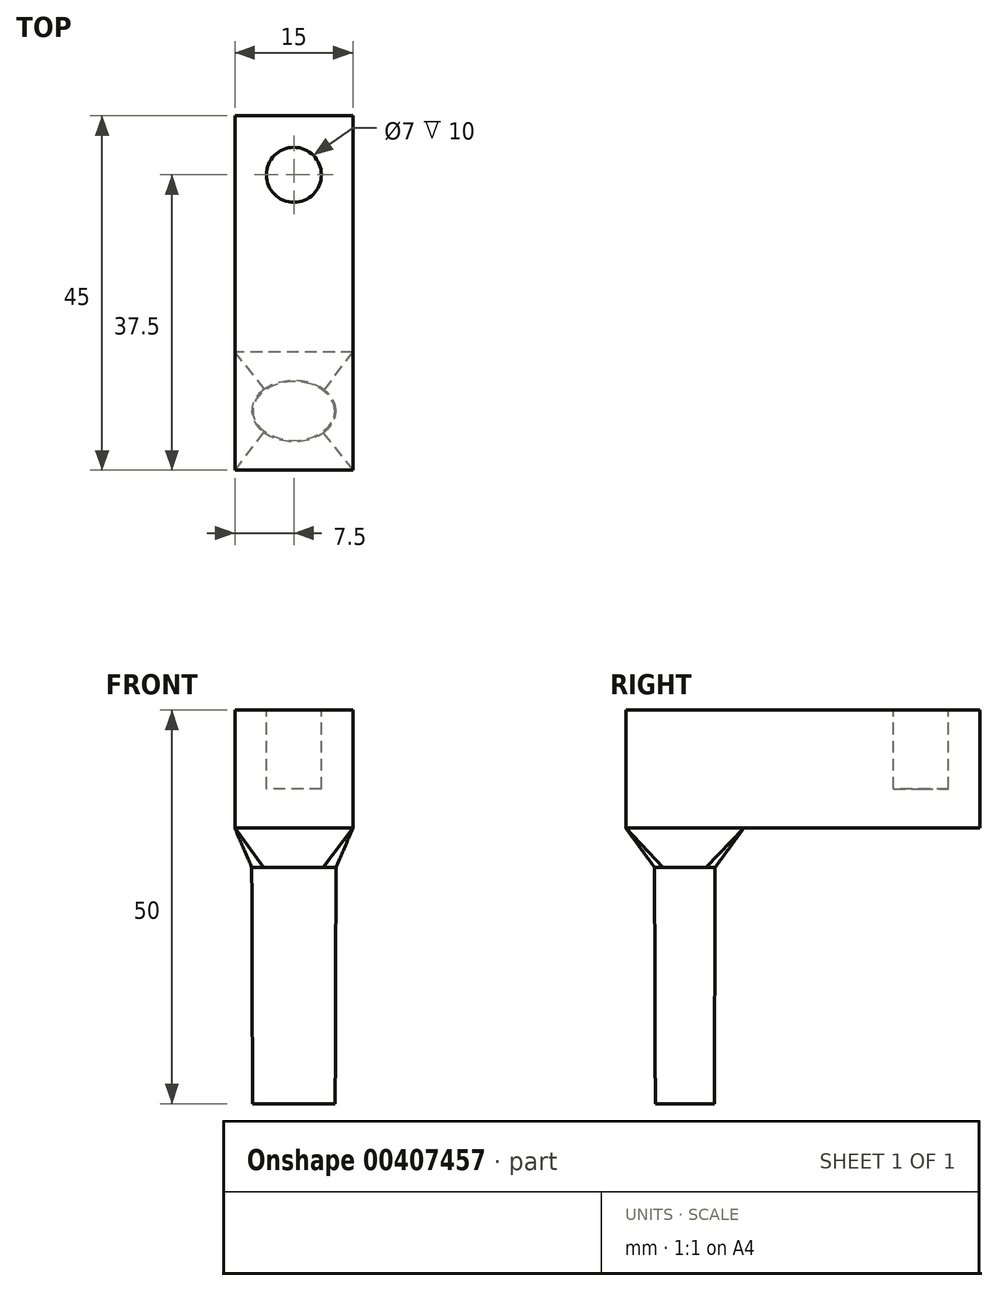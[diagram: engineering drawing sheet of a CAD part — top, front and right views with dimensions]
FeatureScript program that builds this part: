
annotation { "Feature Type Name" : "Feature", "Feature Type Description" : "" }
export const myFeature = defineFeature(function(context is Context, id is Id, definition is map)
    precondition{}
    {
        {
            var Q0;
            Q0=qCreatedBy(makeId("Top.planeOp"),FACE);
            var sketch = newSketch(context, id + "F0", { "sketchPlane" : qUnion([Q0])});
            skEllipse(sketch, "E0", {"center": v(0, 0) * mm, "majorRadius": 5.25 * mm, "minorRadius": 3.75 * mm, "majorAxis": v(1, 0)});
            skSolve(sketch);
        }
        {
            var Q0;
            Q0=qCreatedBy(makeId("Top.planeOp"),FACE);
            cPlane(context, id + "F1", {"entities" : qUnion([Q0]), "cplaneType" : CPlaneType.OFFSET, "offset" : 30 * mm, "width" : 150 * mm, "height" : 150 * mm});
        }
        {
            var Q0;
            Q0=qCreatedBy(id+"F1.planeOp",FACE);
            var sketch = newSketch(context, id + "F2", { "sketchPlane" : qUnion([Q0])});
            skEllipse(sketch, "E1", {"center": v(0, 0) * mm, "majorRadius": 5.35 * mm, "minorRadius": 3.85 * mm, "majorAxis": v(1, 0)});
            skSolve(sketch);
        }
        {
            var Q0;
            Q0 = qSketchRegion(id + "F0", true);
            var Q1;
            Q1 = qSketchRegion(id + "F2", true);
            loft(context, id + "F3", {"sheetProfilesArray" : [{ "sheetProfileEntities" : qUnion([Q0]) }, { "sheetProfileEntities" : qUnion([Q1]) }]});
        }
        {
            var Q0;
            Q0=qCreatedBy(id+"F1.planeOp",FACE);
            cPlane(context, id + "F4", {"entities" : qUnion([Q0]), "cplaneType" : CPlaneType.OFFSET, "offset" : 5 * mm, "width" : 150 * mm, "height" : 150 * mm});
        }
        {
            var Q0;
            Q0=qCreatedBy(id+"F4.planeOp",FACE);
            var sketch = newSketch(context, id + "F5", { "sketchPlane" : qUnion([Q0])});
            skLineSegment(sketch, "E2.bottom", {"start": v(7.5, 7.5) * mm, "end": v(-7.5, 7.5) * mm});
            skLineSegment(sketch, "E2.top", {"start": v(7.5, -7.5) * mm, "end": v(-7.5, -7.5) * mm});
            skLineSegment(sketch, "E2.left", {"start": v(7.5, 7.5) * mm, "end": v(7.5, -7.5) * mm});
            skLineSegment(sketch, "E2.right", {"start": v(-7.5, 7.5) * mm, "end": v(-7.5, -7.5) * mm});
            skPoint(sketch, "E2.middle", {"position": v(0, 0) * mm});
            skSolve(sketch);
        }
        {
            var Q0;
            Q0=makeQuery(id+"F5.imprint","IMPRINT",FACE,{"disambiguationData":[TD([[makeQuery(id+"F5.imprint","IMPRINT",EDGE,{"derivedFrom":sQuery(id+"F5.wireOp",EDGE,"E2.bottom")}),1.0]])]});
            extrude(context, id + "F6", {"entities" : qUnion([Q0]), "depth" : 15 * mm});
        }
        {
            var Q0;
            Q0=makeQuery(id+"F6.opExtrude","SWEPT_FACE",FACE,{"disambiguationData":[OSD([sQuery(id+"F5.wireOp",EDGE,"E2.bottom")])]});
            extrude(context, id + "F7", {"entities" : qUnion([Q0]), "operationType" : NewBodyOperationType.ADD, "depth" : 30 * mm});
        }
        {
            var Q1;
            Q1=makeQuery(id+"F2.imprint","IMPRINT",FACE,{"disambiguationData":[TD([[makeQuery(id+"F2.imprint","IMPRINT",EDGE,{"derivedFrom":sQuery(id+"F2.wireOp",EDGE,"E1")}),1.0]])]});
            var Q2;
            Q2=makeQuery(id+"F5.imprint","IMPRINT",FACE,{"disambiguationData":[TD([[makeQuery(id+"F5.imprint","IMPRINT",EDGE,{"derivedFrom":sQuery(id+"F5.wireOp",EDGE,"E2.bottom")}),1.0]])]});
            loft(context, id + "F8", {"operationType" : NewBodyOperationType.ADD, "sheetProfilesArray" : [{ "sheetProfileEntities" : qUnion([Q1]) }, { "sheetProfileEntities" : qUnion([Q2]) }]});
        }
        {
            var Q0;
            {var subQ0=sQuery(id+"F5.wireOp",EDGE,"E2.bottom");Q0=makeQuery(id+"F7.boolean.opBoolean","MERGE",FACE,{"derivedFrom":[makeQuery(id+"F6.opExtrude","CAP_FACE",FACE,{"disambiguationData":[OSD([subQ0,sQuery(id+"F5.wireOp",EDGE,"E2.top"),sQuery(id+"F5.wireOp",EDGE,"E2.left"),sQuery(id+"F5.wireOp",EDGE,"E2.right")])],"isStart":false}),makeQuery(id+"F7.opExtrude","SWEPT_FACE",FACE,{"disambiguationData":[OSD([subQ0]),TDD([makeQuery(id+"F6.opExtrude","CAP_EDGE",EDGE,{"disambiguationData":[OSD([subQ0])],"isStart":false})])]})]});}
            var sketch = newSketch(context, id + "F9", { "sketchPlane" : qUnion([Q0])});
            skLineSegment(sketch, "E3", {"start": v(7.5, 37.5) * mm, "end": v(-7.5, 22.5) * mm, "construction": true});
            skCircle(sketch, "E4", {"center": v(0, 30) * mm, "radius": 3.5 * mm});
            skSolve(sketch);
        }
        {
            var Q0;
            Q0=makeQuery(id+"F9.imprint","IMPRINT",FACE,{"disambiguationData":[TD([[makeQuery(id+"F9.imprint","IMPRINT",EDGE,{"derivedFrom":sQuery(id+"F9.wireOp",EDGE,"E4")}),1.0]])]});
            extrude(context, id + "F10", {"entities" : qUnion([Q0]), "operationType" : NewBodyOperationType.REMOVE, "oppositeDirection" : true, "depth" : 10 * mm});
        }
    });
